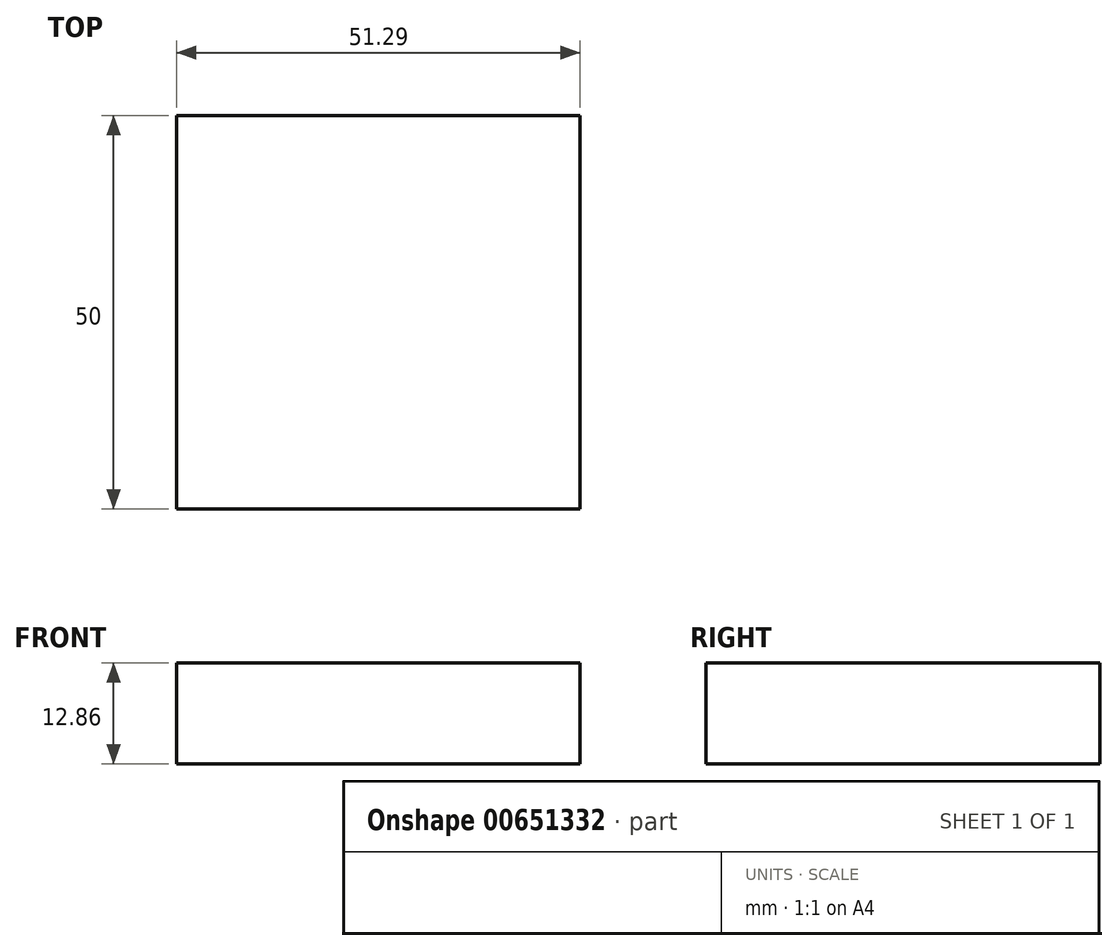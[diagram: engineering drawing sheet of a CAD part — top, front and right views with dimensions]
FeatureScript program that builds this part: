
annotation { "Feature Type Name" : "Feature", "Feature Type Description" : "" }
export const myFeature = defineFeature(function(context is Context, id is Id, definition is map)
    precondition{}
    {
        {
            var Q0;
            Q0=qCreatedBy(makeId("Front.planeOp"),FACE);
            var sketch = newSketch(context, id + "F0", { "sketchPlane" : qUnion([Q0])});
            skLineSegment(sketch, "E0", {"start": v(0, 0) * mm, "end": v(0, 43.46) * mm});
            skSolve(sketch);
        }
        {
            var Q0;
            Q0=qCreatedBy(makeId("Front.planeOp"),FACE);
            var sketch = newSketch(context, id + "F1", { "sketchPlane" : qUnion([Q0])});
            skArc(sketch, "E1", {"start": v(0, 0) * mm, "mid": v(21.87, 21.74) * mm, "end": v(0, 43.48) * mm});
            skSolve(sketch);
        }
        {
            var Q0;
            Q0=sQuery(id+"F1.wireOp",EDGE,"E1");
            var Q1;
            Q1=sQuery(id+"F0.wireOp",EDGE,"E0");
            revolve(context, id + "F2", {"bodyType" : ToolBodyType.SURFACE, "surfaceEntities" : qUnion([Q0]), "axis" : qUnion([Q1]), "revolveType" : RevolveType.FULL});
        }
        {
            var Q0;
            Q0=qCreatedBy(makeId("Front.planeOp"),FACE);
            var sketch = newSketch(context, id + "F3", { "sketchPlane" : qUnion([Q0])});
            skLineSegment(sketch, "E2.bottom", {"start": v(25.92, 0) * mm, "end": v(-25.37, 0) * mm});
            skLineSegment(sketch, "E2.top", {"start": v(25.92, -12.86) * mm, "end": v(-25.37, -12.86) * mm});
            skLineSegment(sketch, "E2.left", {"start": v(25.92, 0) * mm, "end": v(25.92, -12.86) * mm});
            skLineSegment(sketch, "E2.right", {"start": v(-25.37, 0) * mm, "end": v(-25.37, -12.86) * mm});
            skSolve(sketch);
        }
        {
            var Q0;
            Q0 = qSketchRegion(id + "FczpreNKdhajlkI_0", true);
            var Q1;
            Q1=makeQuery(id+"F3.imprint","IMPRINT",FACE,{"disambiguationData":[TD([[makeQuery(id+"F3.imprint","IMPRINT",EDGE,{"derivedFrom":sQuery(id+"F3.wireOp",EDGE,"E2.bottom")}),1.0]])]});
            extrude(context, id + "F4", {"entities" : qUnion([Q0, Q1]), "depth" : 25 * mm, "offsetDistance" : 25 * mm});
        }
        {
            var Q0;
            Q0=makeQuery(id+"F4.opExtrude","CAP_FACE",FACE,{"disambiguationData":[OSD([sQuery(id+"F3.wireOp",EDGE,"E2.bottom"),sQuery(id+"F3.wireOp",EDGE,"E2.top"),sQuery(id+"F3.wireOp",EDGE,"E2.left"),sQuery(id+"F3.wireOp",EDGE,"E2.right")])],"isStart":true});
            var sketch = newSketch(context, id + "F5", { "sketchPlane" : qUnion([Q0])});
            skSolve(sketch);
        }
        {
            var Q0;
            Q0=makeQuery(id+"F5.imprint","IMPRINT",FACE,{"disambiguationData":[TD([[makeQuery(id+"F5.imprint","IMPRINT",EDGE,{"derivedFrom":makeQuery(id+"F4.opExtrude","CAP_EDGE",EDGE,{"disambiguationData":[OSD([sQuery(id+"F3.wireOp",EDGE,"E2.bottom")])],"isStart":true})}),-1.0]])]});
            extrude(context, id + "F6", {"entities" : qUnion([Q0]), "operationType" : NewBodyOperationType.ADD, "depth" : 25 * mm, "offsetDistance" : 25 * mm});
        }
    });
